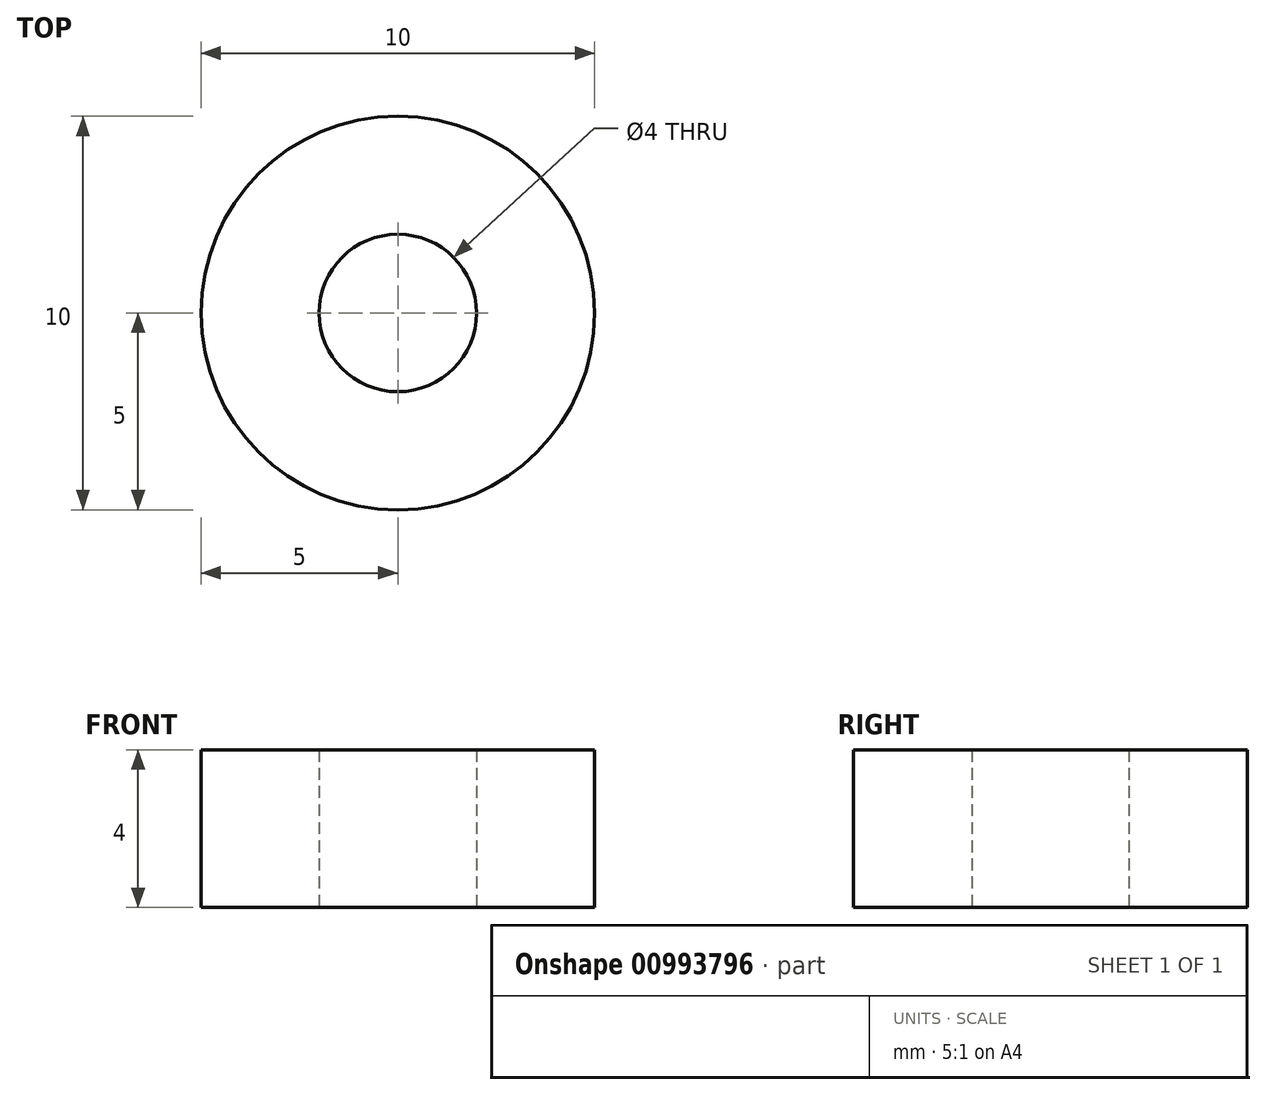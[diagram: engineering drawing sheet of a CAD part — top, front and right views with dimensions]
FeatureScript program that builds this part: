
annotation { "Feature Type Name" : "Feature", "Feature Type Description" : "" }
export const myFeature = defineFeature(function(context is Context, id is Id, definition is map)
    precondition{}
    {
        {
            var Q0;
            Q0=qCreatedBy(makeId("Top.planeOp"),FACE);
            var sketch = newSketch(context, id + "F0", { "sketchPlane" : qUnion([Q0])});
            skCircle(sketch, "E0", {"center": v(0, 0) * mm, "radius": 2 * mm});
            skCircle(sketch, "E1", {"center": v(0, 0) * mm, "radius": 5 * mm});
            skSolve(sketch);
        }
        {
            var Q0;
            Q0=makeQuery(id+"F0.imprint","IMPRINT",FACE,{"disambiguationData":[TD([[makeQuery(id+"F0.imprint","IMPRINT",EDGE,{"derivedFrom":sQuery(id+"F0.wireOp",EDGE,"E0")}),-1.0]])]});
            extrude(context, id + "F1", {"entities" : qUnion([Q0]), "depth" : 4 * mm, "offsetDistance" : 25 * mm});
        }
    });
